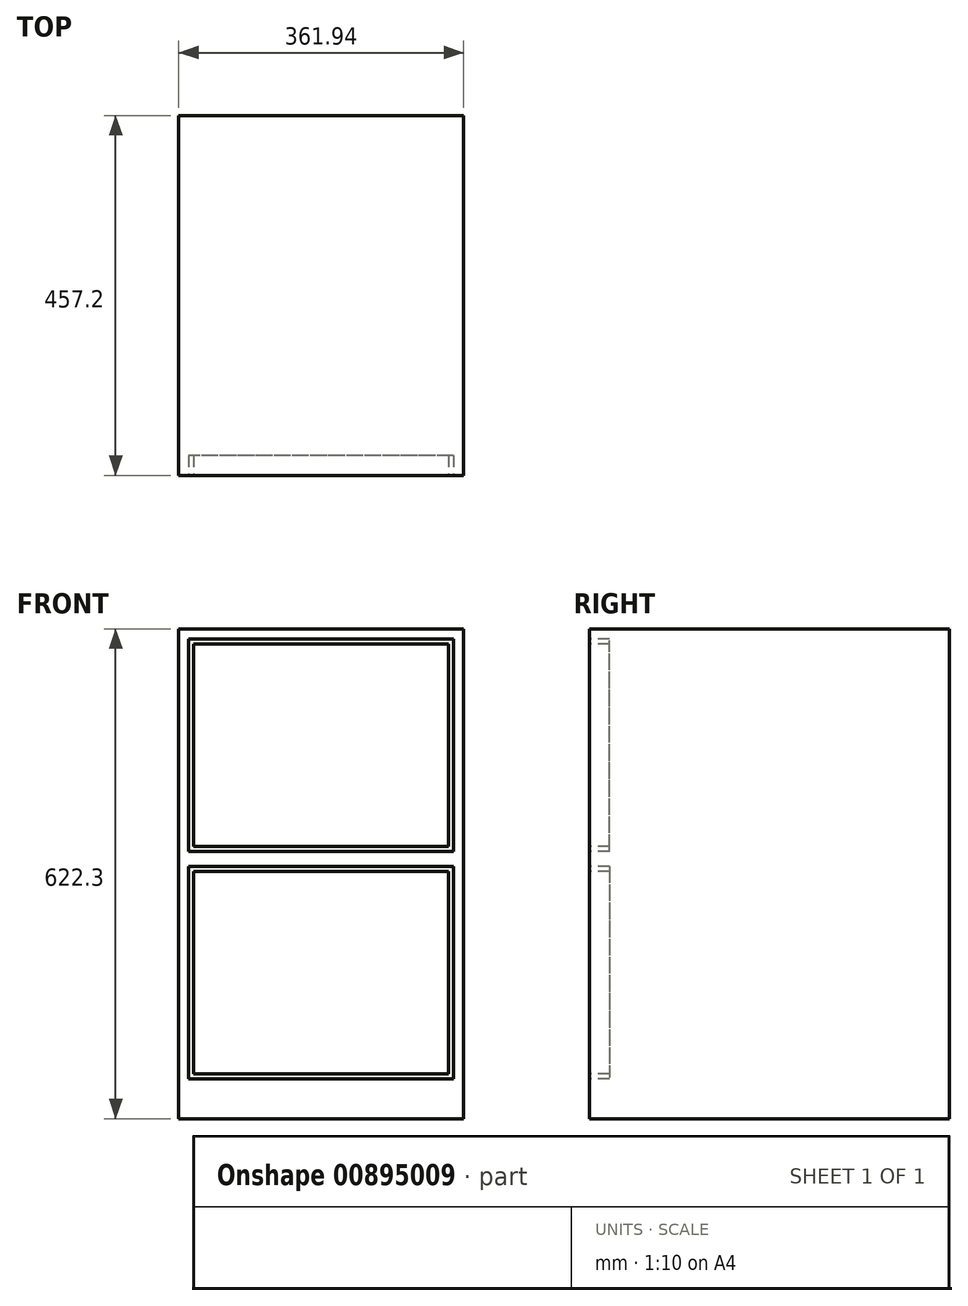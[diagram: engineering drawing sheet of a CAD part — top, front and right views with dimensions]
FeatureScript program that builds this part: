
annotation { "Feature Type Name" : "Feature", "Feature Type Description" : "" }
export const myFeature = defineFeature(function(context is Context, id is Id, definition is map)
    precondition{}
    {
        {
            var Q0;
            Q0=qCreatedBy(makeId("Front.planeOp"),FACE);
            var sketch = newSketch(context, id + "F0", { "sketchPlane" : qUnion([Q0])});
            skLineSegment(sketch, "E0.bottom", {"start": v(-180.97, 311.15) * mm, "end": v(180.98, 311.15) * mm});
            skLineSegment(sketch, "E0.top", {"start": v(-180.97, -311.15) * mm, "end": v(180.97, -311.15) * mm});
            skLineSegment(sketch, "E0.left", {"start": v(-180.97, 311.15) * mm, "end": v(-180.98, -311.15) * mm});
            skLineSegment(sketch, "E0.right", {"start": v(180.98, 311.15) * mm, "end": v(180.97, -311.15) * mm});
            skPoint(sketch, "E0.middle", {"position": v(0, 0) * mm});
            skSolve(sketch);
        }
        {
            var Q0;
            Q0 = qSketchRegion(id + "F0", true);
            extrude(context, id + "F1", {"entities" : qUnion([Q0]), "depth" : 457.2 * mm, "offsetDistance" : 25.4 * mm, "symmetric" : true});
        }
        {
            var Q0;
            Q0=makeQuery(id+"F1.opExtrude","CAP_FACE",FACE,{"disambiguationData":[OSD([sQuery(id+"F0.wireOp",EDGE,"E0.bottom"),sQuery(id+"F0.wireOp",EDGE,"E0.top"),sQuery(id+"F0.wireOp",EDGE,"E0.left"),sQuery(id+"F0.wireOp",EDGE,"E0.right")])],"isStart":false});
            var sketch = newSketch(context, id + "F2", { "sketchPlane" : qUnion([Q0])});
            skLineSegment(sketch, "E1.bottom", {"start": v(168.28, 28.58) * mm, "end": v(-168.28, 28.58) * mm});
            skLineSegment(sketch, "E1.top", {"start": v(168.28, 298.45) * mm, "end": v(-168.28, 298.45) * mm});
            skLineSegment(sketch, "E1.left", {"start": v(168.28, 28.58) * mm, "end": v(168.28, 298.45) * mm});
            skLineSegment(sketch, "E1.right", {"start": v(-168.28, 28.58) * mm, "end": v(-168.28, 298.45) * mm});
            skPoint(sketch, "E1.middle", {"position": v(0, 163.51) * mm});
            skLineSegment(sketch, "E2.bottom", {"start": v(168.28, 9.53) * mm, "end": v(-168.28, 9.53) * mm});
            skLineSegment(sketch, "E2.top", {"start": v(168.28, -260.35) * mm, "end": v(-168.28, -260.35) * mm});
            skLineSegment(sketch, "E2.left", {"start": v(168.28, 9.53) * mm, "end": v(168.28, -260.35) * mm});
            skLineSegment(sketch, "E2.right", {"start": v(-168.28, 9.53) * mm, "end": v(-168.28, -260.35) * mm});
            skPoint(sketch, "E2.middle", {"position": v(0, -125.41) * mm});
            skLineSegment(sketch, "E3.bottom", {"start": v(161.93, 3.18) * mm, "end": v(-161.93, 3.18) * mm});
            skLineSegment(sketch, "E3.top", {"start": v(161.93, -254) * mm, "end": v(-161.93, -254) * mm});
            skLineSegment(sketch, "E3.left", {"start": v(161.93, 3.18) * mm, "end": v(161.93, -254) * mm});
            skLineSegment(sketch, "E3.right", {"start": v(-161.93, 3.18) * mm, "end": v(-161.93, -254) * mm});
            skLineSegment(sketch, "E4.bottom", {"start": v(161.93, 34.93) * mm, "end": v(-161.93, 34.93) * mm});
            skLineSegment(sketch, "E4.top", {"start": v(161.93, 292.1) * mm, "end": v(-161.93, 292.1) * mm});
            skLineSegment(sketch, "E4.left", {"start": v(161.93, 34.93) * mm, "end": v(161.93, 292.1) * mm});
            skLineSegment(sketch, "E4.right", {"start": v(-161.93, 34.93) * mm, "end": v(-161.93, 292.1) * mm});
            skSolve(sketch);
        }
        {
            var Q0;
            Q0 = qSketchRegion(id + "F2", true);
            extrude(context, id + "F3", {"entities" : qUnion([Q0]), "operationType" : NewBodyOperationType.REMOVE, "oppositeDirection" : true, "depth" : 25.4 * mm, "offsetDistance" : 25.4 * mm});
        }
    });
